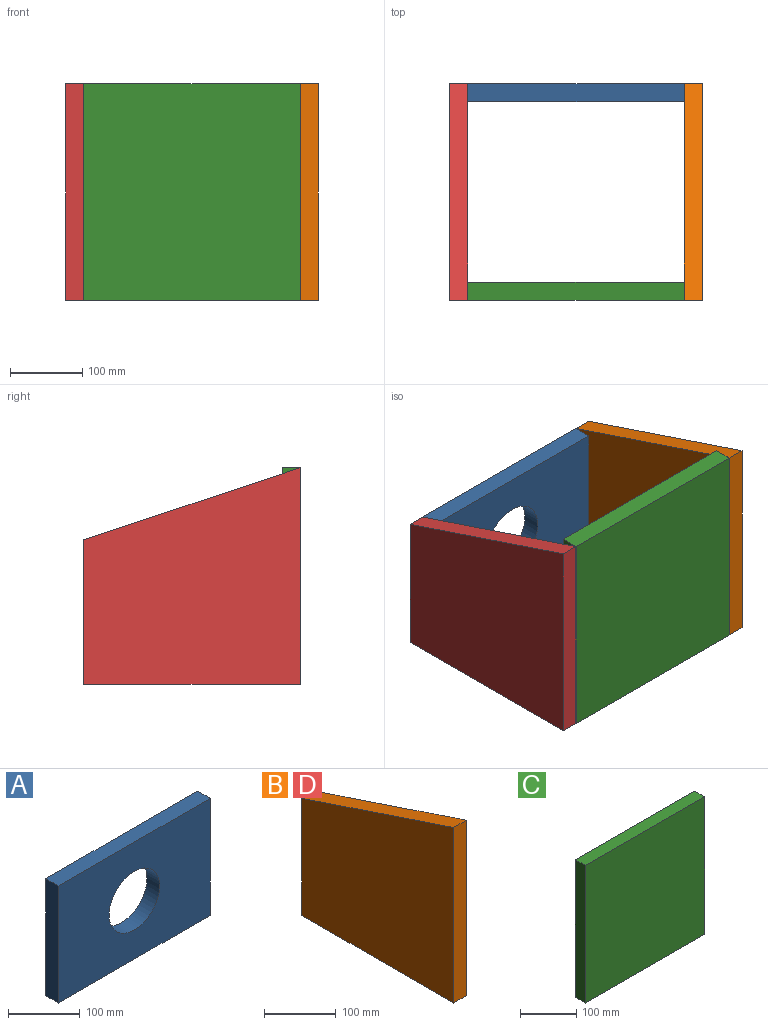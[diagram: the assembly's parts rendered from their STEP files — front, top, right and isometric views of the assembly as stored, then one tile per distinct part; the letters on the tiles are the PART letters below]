
ASSEMBLY  parts=4 mates=3
PART A: 7 faces, bbox 300x25x200 mm
  f0: plane 300x25mm, normal (0,0,1), area 7500mm2, adj f1,f4,f5,f6
  f1: plane 200x25mm, normal (-1,0,0), area 5000mm2, adj f0,f2,f5,f6
  f2: plane 300x25mm, normal (0,0,-1), area 7500mm2, adj f1,f4,f5,f6
  f3: cylinder r=50mm len=100mm, axis (0,1,0), area 7854mm2, adj f5,f6
  f4: plane 200x25mm, normal (1,0,0), area 5000mm2, adj f0,f2,f5,f6
  f5: plane 300x200mm, normal (0,-1,0), area 52146mm2, adj f0,f1,f2,f3,f4
  f6: plane 300x200mm, normal (0,1,0), area 52146mm2, adj f0,f1,f2,f3,f4
PART B: 6 faces, bbox 25x300x300 mm
  f0: plane 300x25mm, normal (0,-1,0), area 7500mm2, adj f1,f3,f4,f5
  f1: plane 300x25mm, normal (0,0,-1), area 7500mm2, adj f0,f2,f4,f5
  f2: plane 200x25mm, normal (0,1,0), area 5000mm2, adj f1,f3,f4,f5
  f3: plane 300x100mm, normal (0,0.32,0.95), area 7905.7mm2, adj f0,f2,f4,f5
  f4: plane 300x300mm, normal (1,0,0), area 75000mm2, adj f0,f1,f2,f3
  f5: plane 300x300mm, normal (-1,0,0), area 75000mm2, adj f0,f1,f2,f3
PART C: 6 faces, bbox 300x25x300 mm
  f0: plane 300x25mm, normal (0,0,1), area 7500mm2, adj f1,f3,f4,f5
  f1: plane 300x25mm, normal (-1,0,0), area 7500mm2, adj f0,f2,f4,f5
  f2: plane 300x25mm, normal (0,0,-1), area 7500mm2, adj f1,f3,f4,f5
  f3: plane 300x25mm, normal (1,0,0), area 7500mm2, adj f0,f2,f4,f5
  f4: plane 300x300mm, normal (0,-1,0), area 90000mm2, adj f0,f1,f2,f3
  f5: plane 300x300mm, normal (0,1,0), area 90000mm2, adj f0,f1,f2,f3
PART D: same geometry as B
PLACE A t=(134.01,341.91,-456.5)mm
PLACE B t=(284.52,190.14,-415.71)mm
PLACE C t=(131.23,66.91,-420.16)mm
PLACE D t=(-40.48,190.14,-415.71)mm
MATE fastened D.f4 <-> A.f1  axis (1,0,0) through (-15.48,341.91,-451.06)mm
MATE fastened D.f4 <-> C.f1  axis (1,0,0) through (-15.48,41.91,-401.06)mm
MATE fastened C.f3 <-> B.f5  axis (1,0,0) through (284.52,41.91,-401.06)mm
